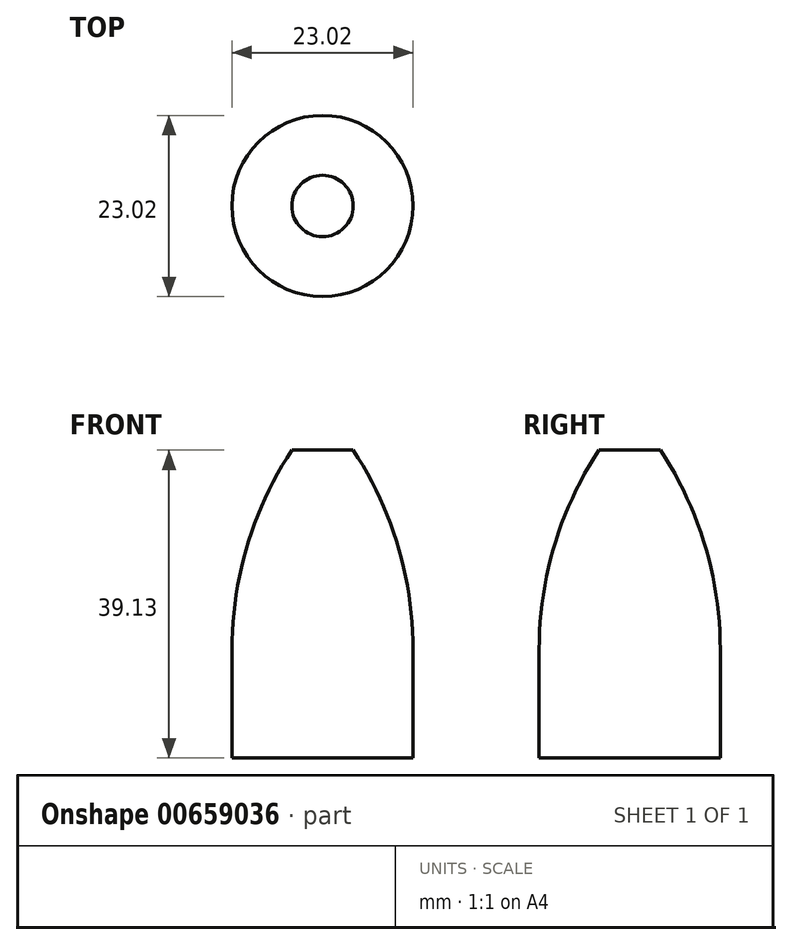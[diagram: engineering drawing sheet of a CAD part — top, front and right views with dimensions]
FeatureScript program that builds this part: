
annotation { "Feature Type Name" : "Feature", "Feature Type Description" : "" }
export const myFeature = defineFeature(function(context is Context, id is Id, definition is map)
    precondition{}
    {
        {
            var Q0;
            Q0=qCreatedBy(makeId("Front.planeOp"),FACE);
            var sketch = newSketch(context, id + "F0", { "sketchPlane" : qUnion([Q0])});
            skLineSegment(sketch, "E0", {"start": v(0, -13.78) * mm, "end": v(11.5, -13.78) * mm});
            skLineSegment(sketch, "E1", {"start": v(11.5, -13.78) * mm, "end": v(11.5, 0) * mm});
            skLineSegment(sketch, "E2", {"start": v(0, 25.35) * mm, "end": v(0, -13.78) * mm});
            skLineSegment(sketch, "E3", {"start": v(0, 45.87) * mm, "end": v(0, -36.07) * mm});
            skLineSegment(sketch, "E4", {"start": v(0, 25.35) * mm, "end": v(3.9, 25.35) * mm});
            skArc(sketch, "E5", {"start": v(11.5, 0) * mm, "mid": v(9.56, 13.23) * mm, "end": v(3.9, 25.35) * mm});
            skSolve(sketch);
        }
        {
            var Q0;
            {var subQ0=sQuery(id+"F0.wireOp",EDGE,"E0");Q0=makeQuery(id+"F0.imprint","IMPRINT",FACE,{"disambiguationData":[TD([[makeQuery(id+"F0.imprint","IMPRINT",EDGE,{"derivedFrom":subQ0}),1.0]])]});}
            var Q1;
            Q1=sQuery(id+"F0.wireOp",EDGE,"E3");
            revolve(context, id + "F1", {"entities" : qUnion([Q0]), "axis" : qUnion([Q1]), "revolveType" : RevolveType.FULL});
        }
    });
